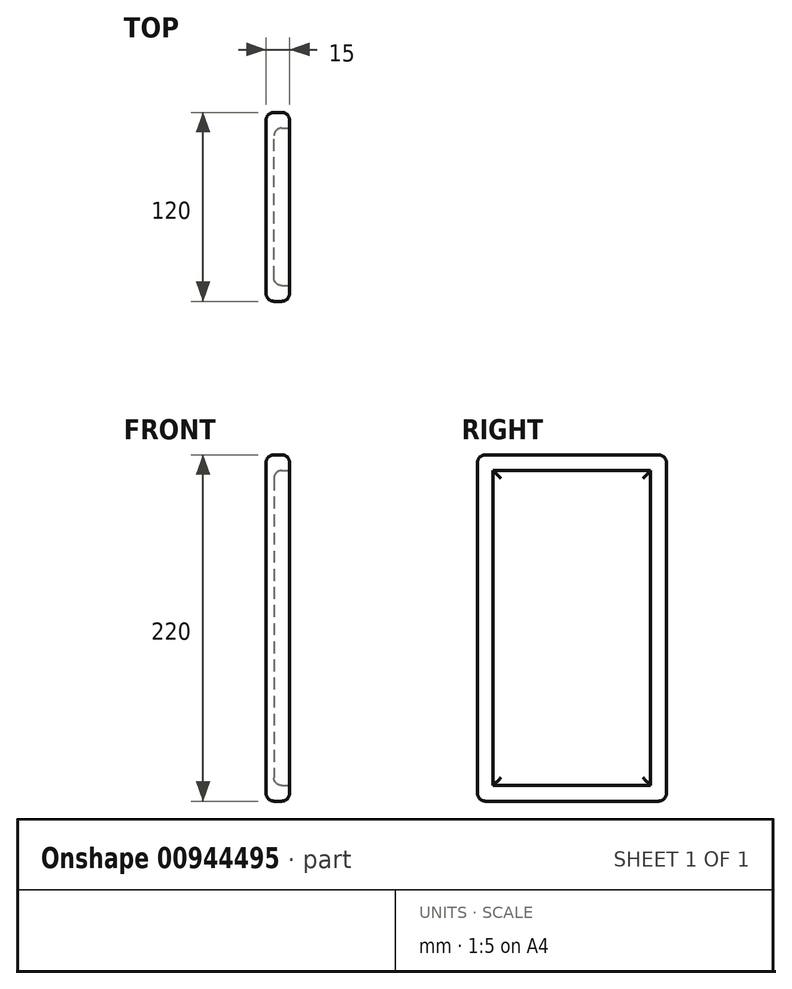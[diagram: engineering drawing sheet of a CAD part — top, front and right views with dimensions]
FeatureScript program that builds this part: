
annotation { "Feature Type Name" : "Feature", "Feature Type Description" : "" }
export const myFeature = defineFeature(function(context is Context, id is Id, definition is map)
    precondition{}
    {
        {
            var Q0;
            Q0=qCreatedBy(makeId("Right.planeOp"),FACE);
            var sketch = newSketch(context, id + "F0", { "sketchPlane" : qUnion([Q0])});
            skLineSegment(sketch, "E0.bottom", {"start": v(0, 0) * mm, "end": v(120, 0) * mm});
            skLineSegment(sketch, "E0.top", {"start": v(0, 220) * mm, "end": v(120, 220) * mm});
            skLineSegment(sketch, "E0.left", {"start": v(0, 0) * mm, "end": v(0, 220) * mm});
            skLineSegment(sketch, "E0.right", {"start": v(120, 0) * mm, "end": v(120, 220) * mm});
            skSolve(sketch);
        }
        {
            var Q0;
            Q0=makeQuery(id+"F0.imprint","IMPRINT",FACE,{"disambiguationData":[TD([[makeQuery(id+"F0.imprint","IMPRINT",EDGE,{"derivedFrom":sQuery(id+"F0.wireOp",EDGE,"AIIV1llE-dQxr-6gYn-A15R-cfJEWbjN9Mwn.bottom")}),-1.0]])]});
            var Q1;
            Q1=makeQuery(id+"F0.imprint","IMPRINT",FACE,{"disambiguationData":[TD([[makeQuery(id+"F0.imprint","IMPRINT",EDGE,{"derivedFrom":sQuery(id+"F0.wireOp",EDGE,"E0.bottom")}),1.0]])]});
            extrude(context, id + "F1", {"entities" : qUnion([Q0, Q1]), "depth" : 15 * mm, "offsetDistance" : 25 * mm});
        }
        {
            var Q0;
            Q0=makeQuery(id+"F1.opExtrude","CAP_FACE",FACE,{"disambiguationData":[OSD([sQuery(id+"F0.wireOp",EDGE,"E0.bottom"),sQuery(id+"F0.wireOp",EDGE,"E0.top"),sQuery(id+"F0.wireOp",EDGE,"E0.left"),sQuery(id+"F0.wireOp",EDGE,"E0.right")])],"isStart":false});
            var sketch = newSketch(context, id + "F2", { "sketchPlane" : qUnion([Q0])});
            skLineSegment(sketch, "E1.bottom", {"start": v(10, 210) * mm, "end": v(110, 210) * mm});
            skLineSegment(sketch, "E1.top", {"start": v(10, 10) * mm, "end": v(110, 10) * mm});
            skLineSegment(sketch, "E1.left", {"start": v(10, 210) * mm, "end": v(10, 10) * mm});
            skLineSegment(sketch, "E1.right", {"start": v(110, 210) * mm, "end": v(110, 10) * mm});
            skSolve(sketch);
        }
        {
            var Q0;
            Q0=makeQuery(id+"F2.imprint","IMPRINT",FACE,{"disambiguationData":[TD([[makeQuery(id+"F2.imprint","IMPRINT",EDGE,{"derivedFrom":sQuery(id+"F2.wireOp",EDGE,"E1.bottom")}),-1.0]])]});
            var Q1;
            Q1=sQuery(id+"F2.wireOp",EDGE,"E1.left");
            var Q2;
            Q2=sQuery(id+"F2.wireOp",EDGE,"E1.bottom");
            var Q3;
            Q3=sQuery(id+"F2.wireOp",EDGE,"E1.right");
            var Q4;
            Q4=sQuery(id+"F2.wireOp",EDGE,"E1.top");
            extrude(context, id + "F3", {"entities" : qUnion([Q0]), "operationType" : NewBodyOperationType.REMOVE, "surfaceEntities" : qUnion([Q1, Q2, Q3, Q4]), "oppositeDirection" : true, "depth" : 10 * mm, "offsetDistance" : 25 * mm});
        }
        {
            var Q0;
            Q0=makeQuery(id+"F3.boolean.opBoolean","COPY",EDGE,{"derivedFrom":makeQuery(id+"F3.opExtrude","CAP_EDGE",EDGE,{"disambiguationData":[OSD([sQuery(id+"F2.wireOp",EDGE,"E1.bottom")])],"isStart":true})});
            var Q1;
            Q1=makeQuery(id+"F3.boolean.opBoolean","COPY",EDGE,{"derivedFrom":makeQuery(id+"F3.opExtrude","CAP_EDGE",EDGE,{"disambiguationData":[OSD([sQuery(id+"F2.wireOp",EDGE,"E1.left")])],"isStart":false})});
            var Q2;
            Q2=makeQuery(id+"F3.boolean.opBoolean","COPY",EDGE,{"derivedFrom":makeQuery(id+"F3.opExtrude","CAP_EDGE",EDGE,{"disambiguationData":[OSD([sQuery(id+"F2.wireOp",EDGE,"E1.right")])],"isStart":true})});
            var Q3;
            Q3=makeQuery(id+"F3.boolean.opBoolean","COPY",EDGE,{"derivedFrom":makeQuery(id+"F3.opExtrude","CAP_EDGE",EDGE,{"disambiguationData":[OSD([sQuery(id+"F2.wireOp",EDGE,"E1.left")])],"isStart":true})});
            var Q4;
            Q4=makeQuery(id+"F3.boolean.opBoolean","COPY",EDGE,{"derivedFrom":makeQuery(id+"F3.opExtrude","CAP_EDGE",EDGE,{"disambiguationData":[OSD([sQuery(id+"F2.wireOp",EDGE,"E1.top")])],"isStart":true})});
            var Q5;
            Q5=makeQuery(id+"F3.boolean.opBoolean","COPY",FACE,{"derivedFrom":makeQuery(id+"F3.opExtrude","CAP_FACE",FACE,{"disambiguationData":[OSD([sQuery(id+"F2.wireOp",EDGE,"E1.bottom"),sQuery(id+"F2.wireOp",EDGE,"E1.top"),sQuery(id+"F2.wireOp",EDGE,"E1.left"),sQuery(id+"F2.wireOp",EDGE,"E1.right")])],"isStart":false})});
            var Q6;
            Q6=makeQuery(id+"F1.opExtrude","CAP_EDGE",EDGE,{"disambiguationData":[OSD([sQuery(id+"F0.wireOp",EDGE,"E0.right")])],"isStart":true});
            var Q7;
            Q7=makeQuery(id+"F1.opExtrude","CAP_EDGE",EDGE,{"disambiguationData":[OSD([sQuery(id+"F0.wireOp",EDGE,"E0.top")])],"isStart":true});
            var Q8;
            Q8=makeQuery(id+"F1.opExtrude","CAP_EDGE",EDGE,{"disambiguationData":[OSD([sQuery(id+"F0.wireOp",EDGE,"E0.left")])],"isStart":true});
            var Q9;
            Q9=makeQuery(id+"F1.opExtrude","CAP_EDGE",EDGE,{"disambiguationData":[OSD([sQuery(id+"F0.wireOp",EDGE,"E0.bottom")])],"isStart":true});
            fillet(context, id + "F4", {"entities" : qUnion([Q0, Q1, Q2, Q3, Q4, Q5, Q6, Q7, Q8, Q9]), "radius" : 5 * mm, "tangentPropagation" : true, "allowEdgeOverflow" : false});
        }
        {
            var Q0;
            Q0=makeQuery(id+"F1.opExtrude","CAP_EDGE",EDGE,{"disambiguationData":[OSD([sQuery(id+"F0.wireOp",EDGE,"E0.left")])],"isStart":false});
            var Q1;
            Q1=makeQuery(id+"F1.opExtrude","CAP_EDGE",EDGE,{"disambiguationData":[OSD([sQuery(id+"F0.wireOp",EDGE,"E0.top")])],"isStart":false});
            var Q2;
            Q2=makeQuery(id+"F1.opExtrude","CAP_EDGE",EDGE,{"disambiguationData":[OSD([sQuery(id+"F0.wireOp",EDGE,"E0.bottom")])],"isStart":false});
            var Q3;
            Q3=makeQuery(id+"F1.opExtrude","CAP_EDGE",EDGE,{"disambiguationData":[OSD([sQuery(id+"F0.wireOp",EDGE,"E0.right")])],"isStart":false});
            var Q4;
            Q4=makeQuery(id+"F1.opExtrude","SWEPT_EDGE",EDGE,{"disambiguationData":[OSD([sQuery(id+"F0.wireOp",EDGE,"E0.top"),sQuery(id+"F0.wireOp",EDGE,"E0.right")])]});
            var Q5;
            Q5=makeQuery(id+"F4.opFillet","BLEND_EDGE",EDGE,{"blendedFrom":[makeQuery(id+"F1.opExtrude","CAP_EDGE",EDGE,{"disambiguationData":[OSD([sQuery(id+"F0.wireOp",EDGE,"E0.top")])],"isStart":true}),makeQuery(id+"F1.opExtrude","CAP_EDGE",EDGE,{"disambiguationData":[OSD([sQuery(id+"F0.wireOp",EDGE,"E0.right")])],"isStart":true})],"blendedInto":[]});
            var Q6;
            Q6=makeQuery(id+"F1.opExtrude","SWEPT_EDGE",EDGE,{"disambiguationData":[OSD([sQuery(id+"F0.wireOp",EDGE,"E0.top"),sQuery(id+"F0.wireOp",EDGE,"E0.left")])]});
            var Q7;
            Q7=makeQuery(id+"F4.opFillet","BLEND_EDGE",EDGE,{"blendedFrom":[makeQuery(id+"F1.opExtrude","CAP_EDGE",EDGE,{"disambiguationData":[OSD([sQuery(id+"F0.wireOp",EDGE,"E0.top")])],"isStart":true}),makeQuery(id+"F1.opExtrude","CAP_EDGE",EDGE,{"disambiguationData":[OSD([sQuery(id+"F0.wireOp",EDGE,"E0.left")])],"isStart":true})],"blendedInto":[]});
            var Q8;
            Q8=makeQuery(id+"F1.opExtrude","SWEPT_EDGE",EDGE,{"disambiguationData":[OSD([sQuery(id+"F0.wireOp",EDGE,"E0.bottom"),sQuery(id+"F0.wireOp",EDGE,"E0.left")])]});
            var Q9;
            {var subQ0=sQuery(id+"F0.wireOp",EDGE,"E0.bottom");Q9=makeQuery(id+"F4.opFillet","BLEND_EDGE",EDGE,{"blendedFrom":[makeQuery(id+"F1.opExtrude","CAP_EDGE",EDGE,{"disambiguationData":[OSD([subQ0])],"isStart":true}),makeQuery(id+"F1.opExtrude","CAP_FACE",FACE,{"disambiguationData":[OSD([subQ0,sQuery(id+"F0.wireOp",EDGE,"E0.top"),sQuery(id+"F0.wireOp",EDGE,"E0.left"),sQuery(id+"F0.wireOp",EDGE,"E0.right")])],"isStart":true})],"blendedInto":[makeQuery(id+"F1.opExtrude","CAP_FACE",FACE,{"disambiguationData":[OSD([subQ0,sQuery(id+"F0.wireOp",EDGE,"E0.top"),sQuery(id+"F0.wireOp",EDGE,"E0.left"),sQuery(id+"F0.wireOp",EDGE,"E0.right")])],"isStart":true})]});}
            var Q10;
            Q10=makeQuery(id+"F1.opExtrude","SWEPT_EDGE",EDGE,{"disambiguationData":[OSD([sQuery(id+"F0.wireOp",EDGE,"E0.bottom"),sQuery(id+"F0.wireOp",EDGE,"E0.right")])]});
            var Q11;
            Q11=makeQuery(id+"F4.opFillet","BLEND_EDGE",EDGE,{"blendedFrom":[makeQuery(id+"F1.opExtrude","CAP_EDGE",EDGE,{"disambiguationData":[OSD([sQuery(id+"F0.wireOp",EDGE,"E0.bottom")])],"isStart":true}),makeQuery(id+"F1.opExtrude","CAP_EDGE",EDGE,{"disambiguationData":[OSD([sQuery(id+"F0.wireOp",EDGE,"E0.right")])],"isStart":true})],"blendedInto":[]});
            fillet(context, id + "F5", {"entities" : qUnion([Q0, Q1, Q2, Q3, Q4, Q5, Q6, Q7, Q8, Q9, Q10, Q11]), "radius" : 5 * mm, "tangentPropagation" : true, "allowEdgeOverflow" : false});
        }
    });
